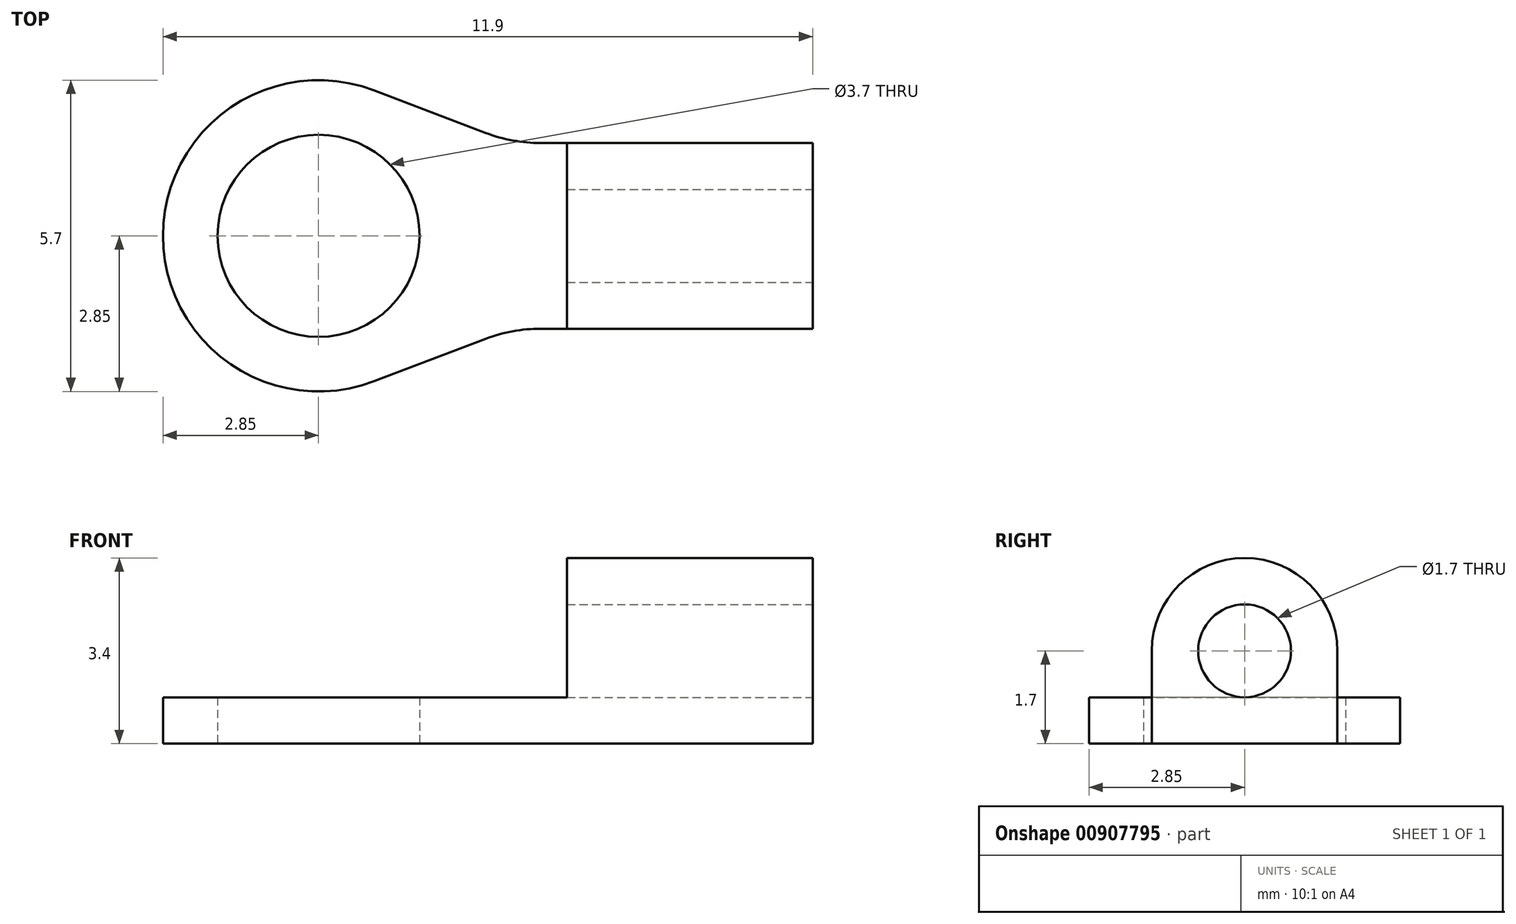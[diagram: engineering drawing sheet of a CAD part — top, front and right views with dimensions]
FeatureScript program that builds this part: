
annotation { "Feature Type Name" : "Feature", "Feature Type Description" : "" }
export const myFeature = defineFeature(function(context is Context, id is Id, definition is map)
    precondition{}
    {
        {
            var Q0;
            Q0=qCreatedBy(makeId("Top.planeOp"),FACE);
            var sketch = newSketch(context, id + "F0", { "sketchPlane" : qUnion([Q0])});
            skLineSegment(sketch, "E0.left", {"start": v(0, 2.85) * mm, "end": v(0, 2.85) * mm});
            skLineSegment(sketch, "E0.right", {"start": v(11.9, 1.15) * mm, "end": v(11.9, 4.55) * mm});
            skPoint(sketch, "E1.visualSharp", {"position": v(0, 5.7) * mm});
            skArc(sketch, "E1.filletArc", {"start": v(2.85, 5.7) * mm, "mid": v(0.83, 4.87) * mm, "end": v(0, 2.85) * mm});
            skPoint(sketch, "E2.visualSharp", {"position": v(0, 0) * mm});
            skArc(sketch, "E2.filletArc", {"start": v(0, 2.85) * mm, "mid": v(0.83, 0.83) * mm, "end": v(2.85, 0) * mm});
            skLineSegment(sketch, "E3.bottom", {"start": v(11.9, 4.55) * mm, "end": v(6.92, 4.55) * mm});
            skLineSegment(sketch, "E3.top", {"start": v(11.9, 1.15) * mm, "end": v(6.92, 1.15) * mm});
            skPoint(sketch, "E3.middle", {"position": v(11.9, 2.85) * mm});
            skArc(sketch, "E4", {"start": v(3.86, 5.51) * mm, "mid": v(0, 2.85) * mm, "end": v(3.86, 0.19) * mm});
            skCircle(sketch, "E5", {"center": v(2.85, 2.85) * mm, "radius": 1.85 * mm});
            skLineSegment(sketch, "E6", {"start": v(5.91, 4.74) * mm, "end": v(3.86, 5.51) * mm});
            skLineSegment(sketch, "E7", {"start": v(5.91, 0.96) * mm, "end": v(3.86, 0.19) * mm});
            skPoint(sketch, "E8.visualSharp", {"position": v(6.4, 1.15) * mm});
            skArc(sketch, "E8.filletArc", {"start": v(6.92, 1.15) * mm, "mid": v(6.4, 1.1) * mm, "end": v(5.91, 0.96) * mm});
            skPoint(sketch, "E9.visualSharp", {"position": v(6.4, 4.55) * mm});
            skArc(sketch, "E9.filletArc", {"start": v(5.91, 4.74) * mm, "mid": v(6.4, 4.6) * mm, "end": v(6.92, 4.55) * mm});
            skPoint(sketch, "E10.orphan", {"position": v(16.4, 4.55) * mm});
            skPoint(sketch, "E11.orphan", {"position": v(16.4, 1.15) * mm});
            skPoint(sketch, "E0.bottom.end.orphan", {"position": v(11.9, 0) * mm});
            skPoint(sketch, "E0.top.end.orphan", {"position": v(11.9, 5.7) * mm});
            skPoint(sketch, "E3.right.end.orphan", {"position": v(7.4, 1.15) * mm});
            skPoint(sketch, "E3.right.start.orphan", {"position": v(7.4, 4.55) * mm});
            skSolve(sketch);
        }
        {
            var Q0;
            Q0=makeQuery(id+"F0.imprint","IMPRINT",FACE,{"disambiguationData":[TD([[makeQuery(id+"F0.imprint","IMPRINT",EDGE,{"derivedFrom":sQuery(id+"F0.wireOp",EDGE,"E0.right")}),1.0]])]});
            extrude(context, id + "F1", {"entities" : qUnion([Q0]), "depth" : 0.85 * mm, "offsetDistance" : 25 * mm});
        }
        {
            var Q0;
            Q0=makeQuery(id+"F1.opExtrude","CAP_FACE",FACE,{"disambiguationData":[OSD([sQuery(id+"F0.wireOp",EDGE,"E0.right"),sQuery(id+"F0.wireOp",EDGE,"E3.bottom"),sQuery(id+"F0.wireOp",EDGE,"E3.top"),sQuery(id+"F0.wireOp",EDGE,"E4"),sQuery(id+"F0.wireOp",EDGE,"E5"),sQuery(id+"F0.wireOp",EDGE,"E6"),sQuery(id+"F0.wireOp",EDGE,"E7"),sQuery(id+"F0.wireOp",EDGE,"E8.filletArc"),sQuery(id+"F0.wireOp",EDGE,"E9.filletArc")])],"isStart":false});
            var sketch = newSketch(context, id + "F2", { "sketchPlane" : qUnion([Q0])});
            skLineSegment(sketch, "E12.bottom", {"start": v(11.9, 4.55) * mm, "end": v(7.4, 4.55) * mm});
            skLineSegment(sketch, "E12.top", {"start": v(11.9, 1.15) * mm, "end": v(7.4, 1.15) * mm});
            skLineSegment(sketch, "E12.left", {"start": v(11.9, 4.55) * mm, "end": v(11.9, 1.15) * mm});
            skLineSegment(sketch, "E12.right", {"start": v(7.4, 4.55) * mm, "end": v(7.4, 1.15) * mm});
            skSolve(sketch);
        }
        {
            var Q0;
            Q0=makeQuery(id+"F2.imprint","IMPRINT",FACE,{"disambiguationData":[TD([[makeQuery(id+"F2.imprint","IMPRINT",EDGE,{"derivedFrom":sQuery(id+"F2.wireOp",EDGE,"E12.bottom")}),1.0]])]});
            extrude(context, id + "F3", {"entities" : qUnion([Q0]), "operationType" : NewBodyOperationType.ADD, "depth" : 2.55 * mm, "offsetDistance" : 25 * mm});
        }
        {
            var Q0;
            Q0=makeQuery(id+"F3.opExtrude","CAP_EDGE",EDGE,{"disambiguationData":[OSD([sQuery(id+"F2.wireOp",EDGE,"E12.bottom")])],"isStart":false});
            var Q1;
            Q1=makeQuery(id+"F3.opExtrude","CAP_EDGE",EDGE,{"disambiguationData":[OSD([sQuery(id+"F2.wireOp",EDGE,"E12.top")])],"isStart":false});
            fillet(context, id + "F4", {"entities" : qUnion([Q0, Q1]), "radius" : 1.7 * mm, "tangentPropagation" : true, "allowEdgeOverflow" : false});
        }
        {
            var Q0;
            Q0=makeQuery(id+"F3.boolean.opBoolean","MERGE",FACE,{"derivedFrom":[makeQuery(id+"F1.opExtrude","SWEPT_FACE",FACE,{"disambiguationData":[OSD([sQuery(id+"F0.wireOp",EDGE,"E0.right")])]}),makeQuery(id+"F3.opExtrude","SWEPT_FACE",FACE,{"disambiguationData":[OSD([sQuery(id+"F2.wireOp",EDGE,"E12.left")])]})]});
            var sketch = newSketch(context, id + "F5", { "sketchPlane" : qUnion([Q0])});
            skCircle(sketch, "E13", {"center": v(2.85, 1.7) * mm, "radius": 0.85 * mm});
            skSolve(sketch);
        }
        {
            var Q0;
            Q0 = qSketchRegion(id + "F5", true);
            extrude(context, id + "F6", {"entities" : qUnion([Q0]), "operationType" : NewBodyOperationType.REMOVE, "oppositeDirection" : true, "depth" : 25 * mm, "offsetDistance" : 25 * mm});
        }
    });
